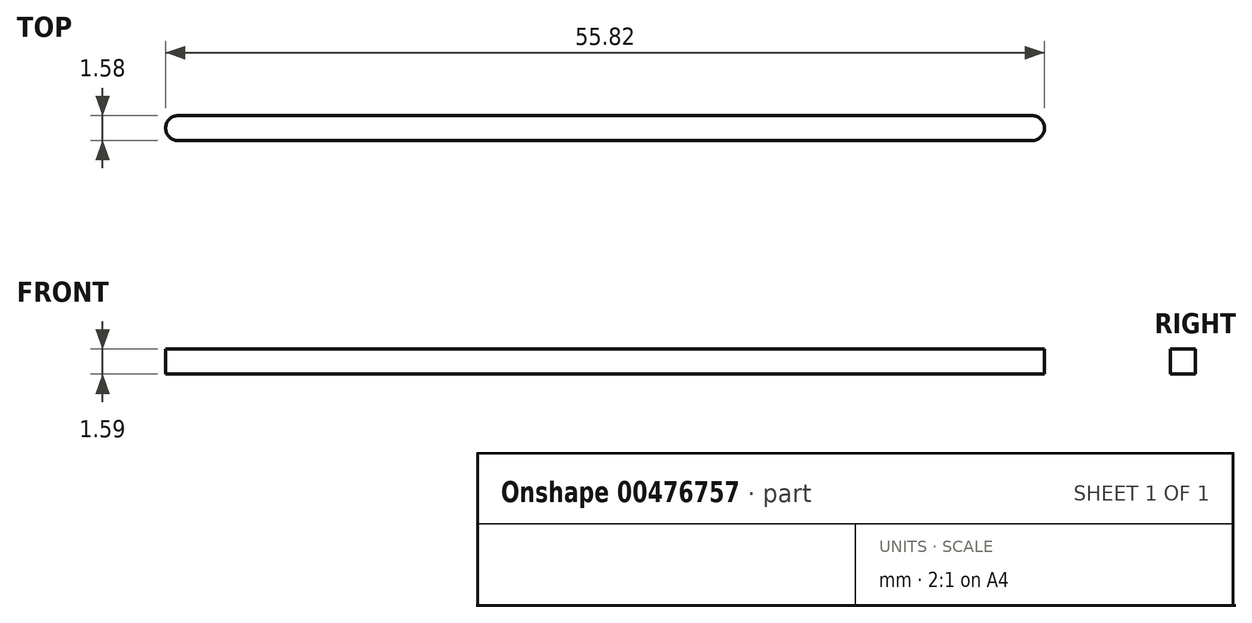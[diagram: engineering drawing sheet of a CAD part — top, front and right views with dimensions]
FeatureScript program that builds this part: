
annotation { "Feature Type Name" : "Feature", "Feature Type Description" : "" }
export const myFeature = defineFeature(function(context is Context, id is Id, definition is map)
    precondition{}
    {
        {
            var Q0;
            Q0=qCreatedBy(makeId("Top.planeOp"),FACE);
            var sketch = newSketch(context, id + "F0", { "sketchPlane" : qUnion([Q0])});
            skLineSegment(sketch, "E0.bottom", {"start": v(27.11, -0.8) * mm, "end": v(-27.11, -0.8) * mm});
            skLineSegment(sketch, "E0.top", {"start": v(27.11, 0.8) * mm, "end": v(-27.11, 0.8) * mm});
            skLineSegment(sketch, "E0.left", {"start": v(27.11, -0.8) * mm, "end": v(27.11, 0.8) * mm});
            skLineSegment(sketch, "E0.right", {"start": v(-27.11, -0.8) * mm, "end": v(-27.11, 0.8) * mm});
            skPoint(sketch, "E0.middle", {"position": v(0, 0) * mm});
            skCircle(sketch, "E1", {"center": v(-27.11, 0) * mm, "radius": 0.8 * mm});
            skCircle(sketch, "E2", {"center": v(27.11, 0) * mm, "radius": 0.8 * mm});
            skSolve(sketch);
        }
        {
            var Q0;
            {var subQ0=sQuery(id+"F0.wireOp",EDGE,"E0.left");Q0=makeQuery(id+"F0.imprint","IMPRINT",FACE,{"disambiguationData":[TD([[makeQuery(id+"F0.imprint","IMPRINT",EDGE,{"derivedFrom":subQ0}),-1.0]])]});}
            var Q1;
            {var subQ0=sQuery(id+"F0.wireOp",EDGE,"E0.left");Q1=makeQuery(id+"F0.imprint","IMPRINT",FACE,{"disambiguationData":[TD([[makeQuery(id+"F0.imprint","IMPRINT",EDGE,{"derivedFrom":subQ0}),1.0]])]});}
            var Q2;
            {var subQ0=sQuery(id+"F0.wireOp",EDGE,"E0.bottom");Q2=makeQuery(id+"F0.imprint","IMPRINT",FACE,{"disambiguationData":[TD([[makeQuery(id+"F0.imprint","IMPRINT",EDGE,{"derivedFrom":subQ0}),-1.0]])]});}
            var Q3;
            {var subQ0=sQuery(id+"F0.wireOp",EDGE,"E0.right");Q3=makeQuery(id+"F0.imprint","IMPRINT",FACE,{"disambiguationData":[TD([[makeQuery(id+"F0.imprint","IMPRINT",EDGE,{"derivedFrom":subQ0}),1.0]])]});}
            var Q4;
            {var subQ0=sQuery(id+"F0.wireOp",EDGE,"E0.right");Q4=makeQuery(id+"F0.imprint","IMPRINT",FACE,{"disambiguationData":[TD([[makeQuery(id+"F0.imprint","IMPRINT",EDGE,{"derivedFrom":subQ0}),-1.0]])]});}
            extrude(context, id + "F1", {"entities" : qUnion([Q0, Q1, Q2, Q3, Q4]), "depth" : 1.59 * mm});
        }
    });
